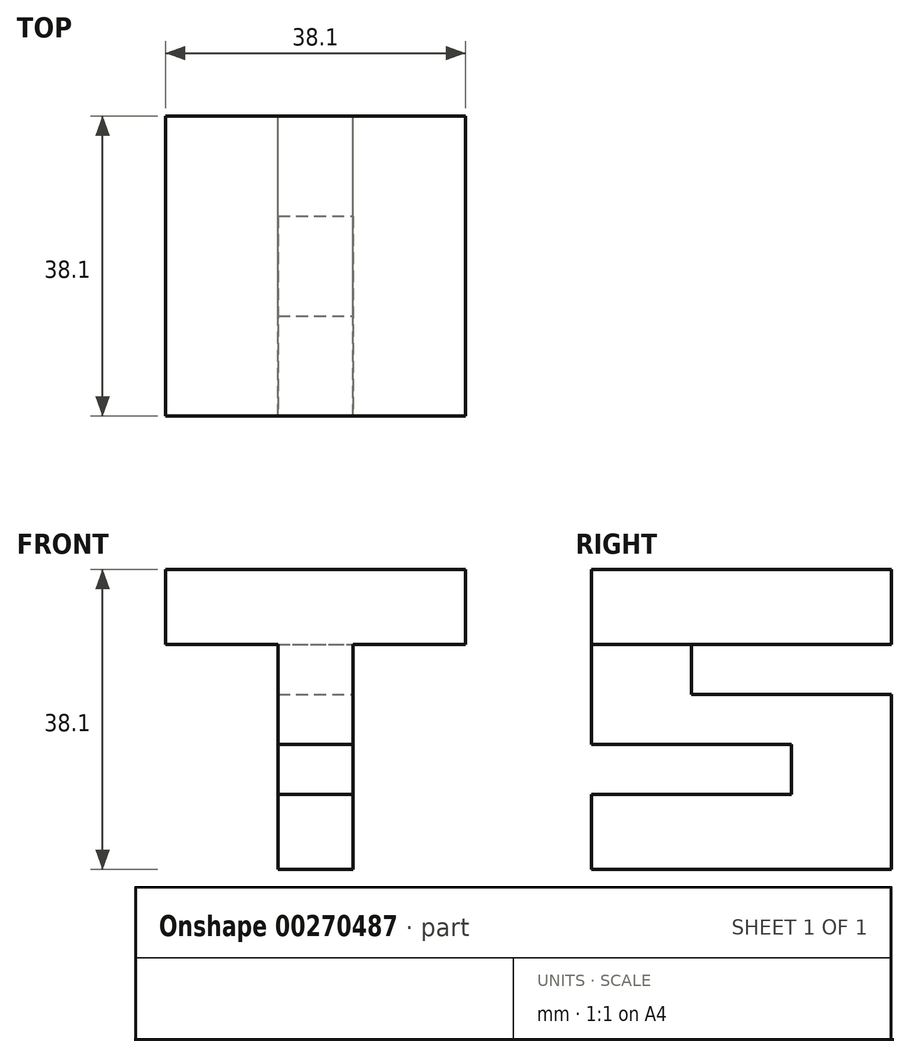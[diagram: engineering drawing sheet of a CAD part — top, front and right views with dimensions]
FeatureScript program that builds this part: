
annotation { "Feature Type Name" : "Feature", "Feature Type Description" : "" }
export const myFeature = defineFeature(function(context is Context, id is Id, definition is map)
    precondition{}
    {
        {
            var Q0;
            Q0=qCreatedBy(makeId("Front.planeOp"),FACE);
            var sketch = newSketch(context, id + "F0", { "sketchPlane" : qUnion([Q0])});
            skLineSegment(sketch, "E0.bottom", {"start": v(0, 38.1) * mm, "end": v(38.1, 38.1) * mm});
            skLineSegment(sketch, "E0.top", {"start": v(0, 28.58) * mm, "end": v(38.1, 28.58) * mm});
            skLineSegment(sketch, "E0.left", {"start": v(0, 38.1) * mm, "end": v(0, 28.57) * mm});
            skLineSegment(sketch, "E0.right", {"start": v(38.1, 38.1) * mm, "end": v(38.1, 28.58) * mm});
            skLineSegment(sketch, "E1.bottom", {"start": v(23.81, 0) * mm, "end": v(14.29, 0) * mm});
            skLineSegment(sketch, "E1.top", {"start": v(23.81, 28.57) * mm, "end": v(14.29, 28.57) * mm});
            skLineSegment(sketch, "E1.left", {"start": v(23.81, 0) * mm, "end": v(23.81, 28.58) * mm});
            skLineSegment(sketch, "E1.right", {"start": v(14.29, 0) * mm, "end": v(14.29, 28.58) * mm});
            skSolve(sketch);
        }
        {
            var Q0;
            Q0=makeQuery(id+"F0.imprint","IMPRINT",FACE,{"disambiguationData":[TD([[makeQuery(id+"F0.imprint","IMPRINT",EDGE,{"derivedFrom":sQuery(id+"F0.wireOp",EDGE,"E0.bottom")}),-1.0]])]});
            var Q1;
            Q1=makeQuery(id+"F0.imprint","IMPRINT",FACE,{"disambiguationData":[TD([[makeQuery(id+"F0.imprint","IMPRINT",EDGE,{"derivedFrom":sQuery(id+"F0.wireOp",EDGE,"E1.bottom")}),-1.0]])]});
            extrude(context, id + "F1", {"entities" : qUnion([Q0, Q1]), "depth" : 38.1 * mm});
        }
        {
            var Q0;
            Q0=makeQuery(id+"F1.opExtrude","SWEPT_FACE",FACE,{"disambiguationData":[OSD([sQuery(id+"F0.wireOp",EDGE,"E0.right")])]});
            var sketch = newSketch(context, id + "F2", { "sketchPlane" : qUnion([Q0])});
            skLineSegment(sketch, "E2.bottom", {"start": v(0, 28.58) * mm, "end": v(-25.4, 28.58) * mm});
            skLineSegment(sketch, "E2.top", {"start": v(0, 22.23) * mm, "end": v(-25.4, 22.23) * mm});
            skLineSegment(sketch, "E2.left", {"start": v(0, 28.58) * mm, "end": v(0, 22.23) * mm});
            skLineSegment(sketch, "E2.right", {"start": v(-25.4, 28.58) * mm, "end": v(-25.4, 22.23) * mm});
            skLineSegment(sketch, "E3.bottom", {"start": v(-38.1, 15.87) * mm, "end": v(-12.7, 15.87) * mm});
            skLineSegment(sketch, "E3.top", {"start": v(-38.1, 9.52) * mm, "end": v(-12.7, 9.52) * mm});
            skLineSegment(sketch, "E3.left", {"start": v(-38.1, 15.87) * mm, "end": v(-38.1, 9.52) * mm});
            skLineSegment(sketch, "E3.right", {"start": v(-12.7, 15.87) * mm, "end": v(-12.7, 9.52) * mm});
            skSolve(sketch);
        }
        {
            var Q0;
            Q0=makeQuery(id+"F2.imprint","IMPRINT",FACE,{"disambiguationData":[TD([[makeQuery(id+"F2.imprint","IMPRINT",EDGE,{"derivedFrom":sQuery(id+"F2.wireOp",EDGE,"E3.bottom")}),-1.0]])]});
            var Q1;
            Q1=makeQuery(id+"F2.imprint","IMPRINT",FACE,{"disambiguationData":[TD([[makeQuery(id+"F2.imprint","IMPRINT",EDGE,{"derivedFrom":sQuery(id+"F2.wireOp",EDGE,"E2.bottom")}),-1.0]])]});
            extrude(context, id + "F3", {"entities" : qUnion([Q0, Q1]), "operationType" : NewBodyOperationType.REMOVE, "oppositeDirection" : true, "depth" : 25.4 * mm});
        }
    });
